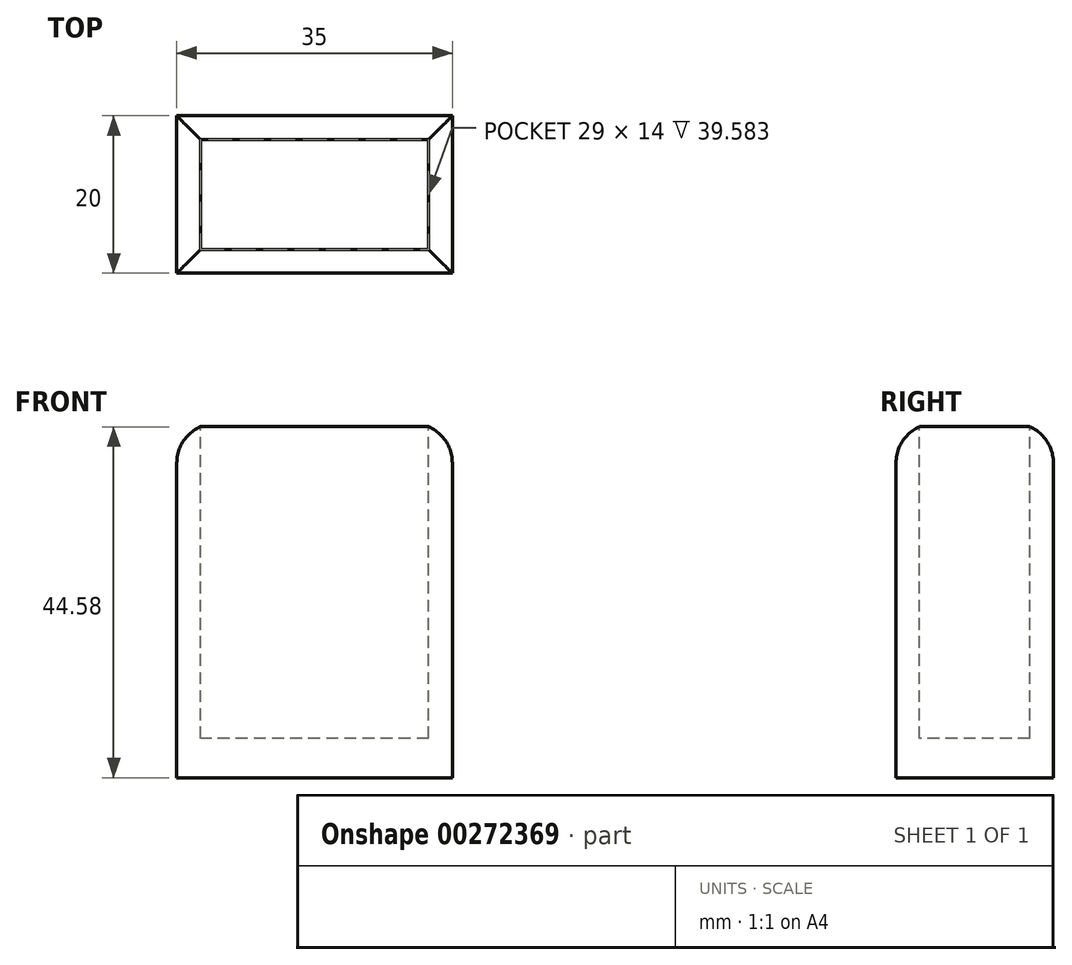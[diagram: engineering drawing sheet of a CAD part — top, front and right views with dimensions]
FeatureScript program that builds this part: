
annotation { "Feature Type Name" : "Feature", "Feature Type Description" : "" }
export const myFeature = defineFeature(function(context is Context, id is Id, definition is map)
    precondition{}
    {
        {
            var Q0;
            Q0=qCreatedBy(makeId("Top.planeOp"),FACE);
            var sketch = newSketch(context, id + "F0", { "sketchPlane" : qUnion([Q0])});
            skLineSegment(sketch, "E0.bottom", {"start": v(-17.5, 10) * mm, "end": v(17.5, 10) * mm});
            skLineSegment(sketch, "E0.top", {"start": v(-17.5, -10) * mm, "end": v(17.5, -10) * mm});
            skLineSegment(sketch, "E0.left", {"start": v(-17.5, 10) * mm, "end": v(-17.5, -10) * mm});
            skLineSegment(sketch, "E0.right", {"start": v(17.5, 10) * mm, "end": v(17.5, -10) * mm});
            skPoint(sketch, "E0.middle", {"position": v(0, 0) * mm});
            skSolve(sketch);
        }
        {
            var Q0;
            Q0 = qSketchRegion(id + "F0", true);
            var Q1;
            Q1 = qSketchRegion(id + "FXrIPOPEhgxDLWn_1", true);
            extrude(context, id + "F1", {"entities" : qUnion([Q0, Q1]), "depth" : 45 * mm});
        }
        {
            var Q0;
            Q0=makeQuery(id+"F1.opExtrude","CAP_FACE",FACE,{"disambiguationData":[OSD([sQuery(id+"F0.wireOp",EDGE,"E0.bottom"),sQuery(id+"F0.wireOp",EDGE,"E0.top"),sQuery(id+"F0.wireOp",EDGE,"E0.left"),sQuery(id+"F0.wireOp",EDGE,"E0.right")])],"isStart":false});
            var sketch = newSketch(context, id + "F2", { "sketchPlane" : qUnion([Q0])});
            skLineSegment(sketch, "E1.0", {"start": v(-14.5, 7) * mm, "end": v(-14.5, -7) * mm});
            skLineSegment(sketch, "E1.1", {"start": v(14.5, 7) * mm, "end": v(-14.5, 7) * mm});
            skLineSegment(sketch, "E1.2", {"start": v(14.5, -7) * mm, "end": v(14.5, 7) * mm});
            skLineSegment(sketch, "E1.3", {"start": v(-14.5, -7) * mm, "end": v(14.5, -7) * mm});
            skSolve(sketch);
        }
        {
            var Q0;
            Q0=makeQuery(id+"F2.imprint","IMPRINT",FACE,{"disambiguationData":[TD([[makeQuery(id+"F2.imprint","IMPRINT",EDGE,{"derivedFrom":sQuery(id+"F2.wireOp",EDGE,"E1.0")}),1.0]])]});
            extrude(context, id + "F3", {"entities" : qUnion([Q0]), "operationType" : NewBodyOperationType.REMOVE, "oppositeDirection" : true, "depth" : 40 * mm});
        }
        {
            var Q0;
            Q0=makeQuery(id+"F1.opExtrude","CAP_EDGE",EDGE,{"disambiguationData":[OSD([sQuery(id+"F0.wireOp",EDGE,"E0.right")])],"isStart":false});
            var Q1;
            Q1=makeQuery(id+"F1.opExtrude","CAP_EDGE",EDGE,{"disambiguationData":[OSD([sQuery(id+"F0.wireOp",EDGE,"E0.top")])],"isStart":false});
            var Q2;
            Q2=makeQuery(id+"F1.opExtrude","CAP_EDGE",EDGE,{"disambiguationData":[OSD([sQuery(id+"F0.wireOp",EDGE,"E0.left")])],"isStart":false});
            var Q3;
            Q3=makeQuery(id+"F1.opExtrude","CAP_EDGE",EDGE,{"disambiguationData":[OSD([sQuery(id+"F0.wireOp",EDGE,"E0.bottom")])],"isStart":false});
            fillet(context, id + "F4", {"entities" : qUnion([Q0, Q1, Q2, Q3]), "radius" : 5 * mm, "tangentPropagation" : true, "allowEdgeOverflow" : false});
        }
    });
